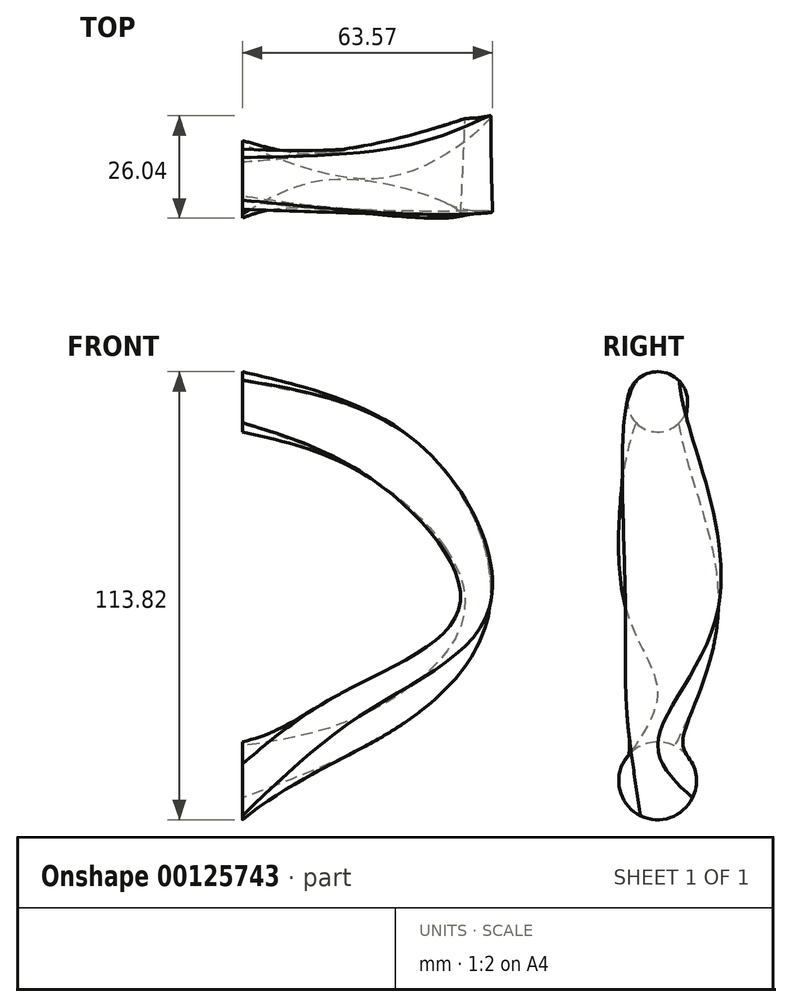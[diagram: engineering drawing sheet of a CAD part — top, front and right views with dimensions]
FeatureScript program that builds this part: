
annotation { "Feature Type Name" : "Feature", "Feature Type Description" : "" }
export const myFeature = defineFeature(function(context is Context, id is Id, definition is map)
    precondition{}
    {
        {
            var Q0;
            Q0=qCreatedBy(makeId("Right.planeOp"),FACE);
            var Q1;
            Q1=qCreatedBy(makeId("Top.planeOp"),FACE);
            cPlane(context, id + "F0", {"entities" : qUnion([Q0, Q1]), "cplaneType" : CPlaneType.MID_PLANE, "offset" : 25.4 * mm, "width" : 152.4 * mm, "height" : 152.4 * mm});
        }
        {
            var Q0;
            Q0=qCreatedBy(makeId("Right.planeOp"),FACE);
            var Q1;
            Q1=qCreatedBy(makeId("Top.planeOp"),FACE);
            cPlane(context, id + "F1", {"entities" : qUnion([Q0, Q1]), "cplaneType" : CPlaneType.MID_PLANE, "offset" : 25.4 * mm, "flipAlignment" : true, "width" : 152.4 * mm, "height" : 152.4 * mm});
        }
        {
            var Q0;
            Q0=qCreatedBy(makeId("Right.planeOp"),FACE);
            var sketch = newSketch(context, id + "F2", { "sketchPlane" : qUnion([Q0])});
            skCircle(sketch, "E0", {"center": v(0, 52.18) * mm, "radius": 7.64 * mm});
            skSolve(sketch);
        }
        {
            var Q0;
            Q0=qCreatedBy(id+"F0.planeOp",FACE);
            var sketch = newSketch(context, id + "F3", { "sketchPlane" : qUnion([Q0])});
            skLineSegment(sketch, "E1.bottom", {"start": v(8.84, 60.8) * mm, "end": v(-8.84, 60.8) * mm});
            skLineSegment(sketch, "E1.top", {"start": v(8.84, 46.22) * mm, "end": v(-8.84, 46.22) * mm});
            skLineSegment(sketch, "E1.left", {"start": v(8.84, 60.8) * mm, "end": v(8.84, 46.22) * mm});
            skLineSegment(sketch, "E1.right", {"start": v(-8.84, 60.8) * mm, "end": v(-8.84, 46.22) * mm});
            skPoint(sketch, "E1.middle", {"position": v(0, 53.5) * mm});
            skSolve(sketch);
        }
        {
            var Q0;
            Q0=qCreatedBy(makeId("Top.planeOp"),FACE);
            var sketch = newSketch(context, id + "F4", { "sketchPlane" : qUnion([Q0])});
            skLineSegment(sketch, "E2.bottom", {"start": v(62.83, 15.44) * mm, "end": v(56.57, 15.44) * mm});
            skLineSegment(sketch, "E2.top", {"start": v(62.83, -8.16) * mm, "end": v(55.15, -8.16) * mm});
            skLineSegment(sketch, "E2.left", {"start": v(62.83, 15.44) * mm, "end": v(62.83, -8.16) * mm});
            skLineSegment(sketch, "E2.right", {"start": v(56.57, 15.44) * mm, "end": v(55.15, -8.16) * mm});
            skSolve(sketch);
        }
        {
            var Q0;
            Q0=qCreatedBy(id+"F1.planeOp",FACE);
            var sketch = newSketch(context, id + "F5", { "sketchPlane" : qUnion([Q0])});
            skCircle(sketch, "E3", {"center": v(0, -40.22) * mm, "radius": 7.67 * mm});
            skSolve(sketch);
        }
        {
            var Q0;
            Q0=qCreatedBy(makeId("Right.planeOp"),FACE);
            var sketch = newSketch(context, id + "F6", { "sketchPlane" : qUnion([Q0])});
            skCircle(sketch, "E4", {"center": v(0, -44.13) * mm, "radius": 9.87 * mm});
            skSolve(sketch);
        }
        {
            var Q0;
            Q0 = qSketchRegion(id + "F2", true);
            var Q1;
            Q1 = qSketchRegion(id + "F3", true);
            var Q2;
            Q2 = qSketchRegion(id + "F4", true);
            var Q3;
            Q3 = qSketchRegion(id + "F5", true);
            var Q4;
            Q4 = qSketchRegion(id + "F6", true);
            loft(context, id + "F7", {"sheetProfilesArray" : [{ "sheetProfileEntities" : qUnion([Q0]) }, { "sheetProfileEntities" : qUnion([Q1]) }, { "sheetProfileEntities" : qUnion([Q2]) }, { "sheetProfileEntities" : qUnion([Q3]) }, { "sheetProfileEntities" : qUnion([Q4]) }]});
        }
    });
